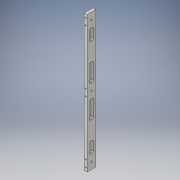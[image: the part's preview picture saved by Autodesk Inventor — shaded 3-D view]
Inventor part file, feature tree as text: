
AUTODESK INVENTOR PART (.ipt)
format: ipt  version: 2019 (Build 230136000, 136)  size: 209,920 bytes
history: native  units: in
note: dims shown in document units (in); Inventor stores cm internally (conversion verified against a paired STEP export)
features: fillet x16, sketch x4, extrude x2, hole x2
ambient origin geometry x8: Origin, YZ Plane, XZ Plane, XY Plane, X Axis, Y Axis, Z Axis, Center Point
bodies: Solid1 (feature_tree)
feature tree (24):
  extrude  "Extrusion1"  Depth=0.75in
  hole  "Hole1"  [1 undecoded]
  extrude  "Extrusion2"  Depth=5.9055in
  fillet  "Fillet1"  Radius=0.5906in
  fillet  "Fillet2"  Radius=0.375in
  fillet  "Fillet3"  Radius=0.375in
  fillet  "Fillet4"  Radius=5.9055in
  fillet  "Fillet5"  Radius=0.1969in
  fillet  "Fillet6"  Radius=0.1969in
  fillet  "Fillet7"  Radius=1.1811in
  fillet  "Fillet8"  Radius=1.1811in
  fillet  "Fillet9"  Radius=2.1654in
  fillet  "Fillet10"  Radius=3.7402in
  fillet  "Fillet11"  Radius=5.315in
  fillet  "Fillet12"  Radius=2.1654in
  fillet  "Fillet13"  Radius=3.7402in
  fillet  "Fillet14"  Radius=5.315in
  fillet  "Fillet15"  Radius=0.25in
  fillet  "Fillet16"  Radius=0.125in
  hole  "Hole3"  [1 undecoded]
  sketch  "Sketch1"  dims[d0=11.811in d1=0.75in]
  sketch  "Sketch2"  dims[d2=0.25in d3=0.0in d4=0.5906in]
  sketch  "Sketch5"  dims[d5=0.75in d6=0.375in d7=0.5906in d8=0.375in d9=0.375in d10=5.9055in]
  sketch  "Sketch7"  dims[d11=0.13in d12=0.328in d13=0.375in d14=0.25in d15=0.5635in d16=0.484in d17=0.8108in d44=0.1969in d45=0.1969in d46=1.1811in d47=1.1811in d48=2.1654in d49=3.7402in d50=5.315in d51=2.1654in d52=3.7402in d53=5.315in d54=0.25in d55=0.0in d56=0.125in d57=0.125in d58=0.125in d59=0.125in d60=0.125in d61=0.125in d62=0.125in d63=0.125in d64=0.125in d65=0.125in d66=0.125in d67=0.125in d68=0.125in d69=0.125in d70=0.125in d71=0.125in d72=0.2953in d73=0.8858in d74=5.6102in d78=0.2953in d79=0.8858in d82=5.6102in d83=0.25in d84=0.125in d85=0.125in d87=0.125in d88=0.125in d89=0.125in d91=0.125in d92=0.125in d93=0.125in d94=0.104in d95=1.0in d96=0.375in d97=0.25in d98=0.5635in d99=0.432in d100=0.0in]
note: 2 required parameter values undecoded (feature->parameter linkage not recoverable at this tier; creation-order binding heuristic only, values carry confidence <= 0.55)
